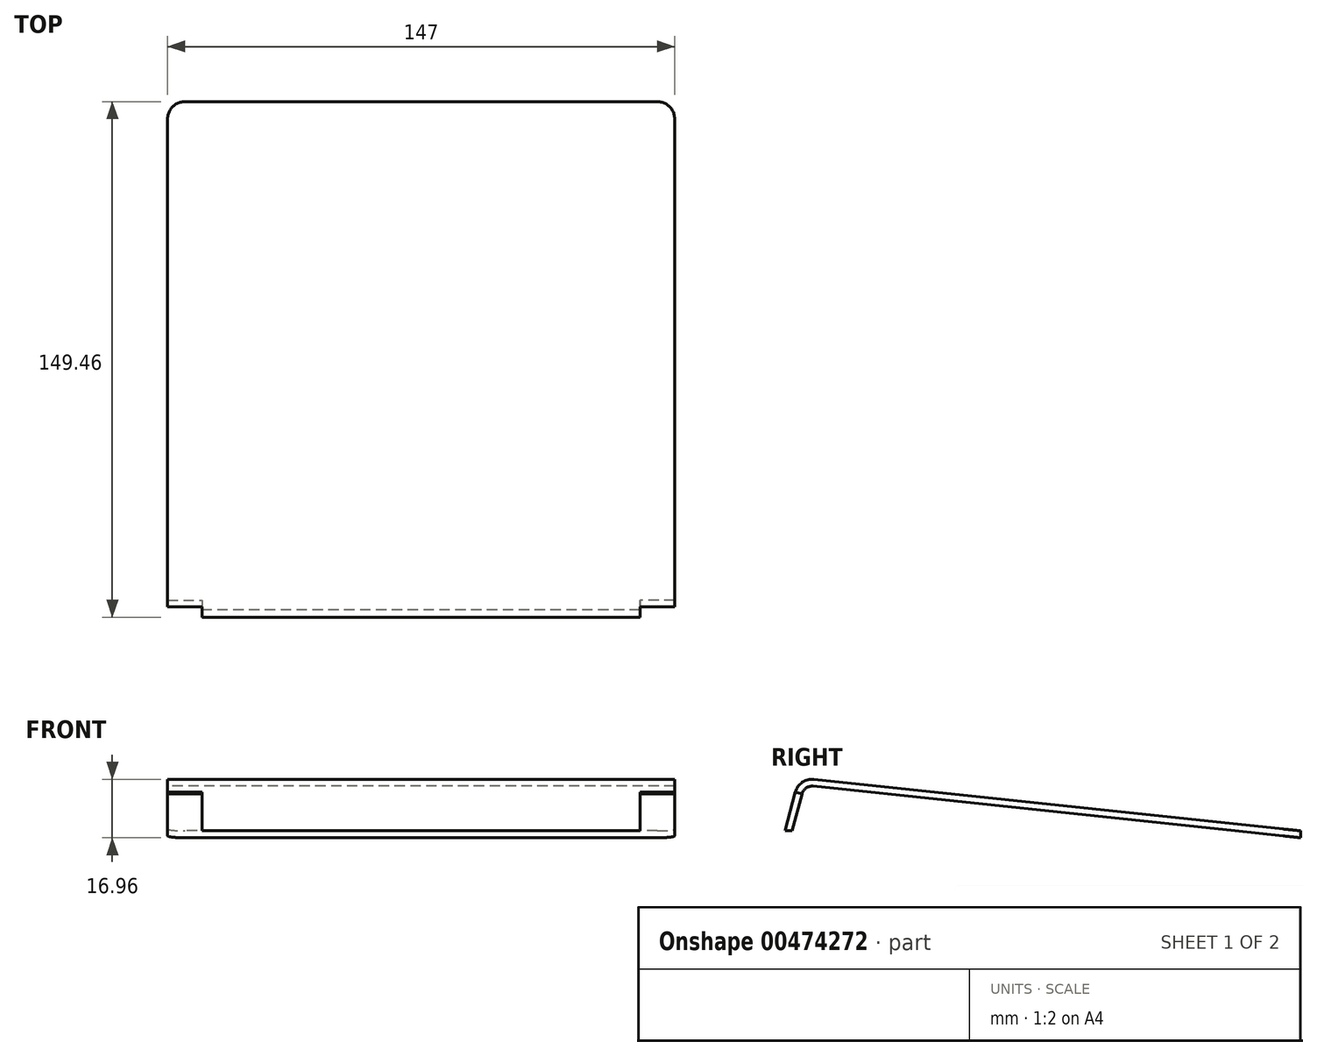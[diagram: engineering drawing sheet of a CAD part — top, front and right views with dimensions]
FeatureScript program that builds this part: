
annotation { "Feature Type Name" : "Feature", "Feature Type Description" : "" }
export const myFeature = defineFeature(function(context is Context, id is Id, definition is map)
    precondition{}
    {
        {
            assignVariable(context, id + "F0", {"name" : "lidWidth", "anyValue" : 129 * mm + 2 * mm});
        }
        {
            assignVariable(context, id + "F1", {"name" : "shellThickness", "anyValue" : 2 * mm});
        }
        {
            var Q0;
            Q0=qCreatedBy(makeId("Right.planeOp"),FACE);
            var sketch = newSketch(context, id + "F2", { "sketchPlane" : qUnion([Q0])});
            skLineSegment(sketch, "E0", {"start": v(-96.45, 13.26) * mm, "end": v(-100, 0) * mm});
            skLineSegment(sketch, "E1", {"start": v(-100, 0) * mm, "end": v(50, 0) * mm});
            skLineSegment(sketch, "E2", {"start": v(50, 0) * mm, "end": v(50, 2) * mm});
            skLineSegment(sketch, "E3", {"start": v(50, 2) * mm, "end": v(-91.1, 16.94) * mm});
            skPoint(sketch, "E4.visualSharp", {"position": v(-95.34, 17.39) * mm});
            skArc(sketch, "E4.filletArc", {"start": v(-91.1, 16.94) * mm, "mid": v(-94.45, 16.09) * mm, "end": v(-96.45, 13.26) * mm});
            skPoint(sketch, "E5", {"position": v(0, 0) * mm});
            skSolve(sketch);
        }
        {
            var Q0;
            Q0 = qSketchRegion(id + "F2", true);
            extrude(context, id + "F3", {"entities" : qUnion([Q0]), "depth" : getVariable(context, 'lidWidth')});
        }
        {
            var Q0;
            Q0=makeQuery(id+"F3.opExtrude","SWEPT_FACE",FACE,{"disambiguationData":[OSD([sQuery(id+"F2.wireOp",EDGE,"E3")])]});
            var Q1;
            Q1=makeQuery(id+"F3.opExtrude","SWEPT_BODY",BODY,{"disambiguationData":[OSD([sQuery(id+"F2.wireOp",EDGE,"E0"),sQuery(id+"F2.wireOp",EDGE,"E2"),sQuery(id+"F2.wireOp",EDGE,"E3"),sQuery(id+"F2.wireOp",EDGE,"E4.filletArc"),sQuery(id+"F2.wireOp",EDGE,"8XllQhxL-LN9K-vVAI-bg7h-7nyJZGlVxFld"),sQuery(id+"F2.wireOp",EDGE,"6OsOoCNm-2A1r-wOlb-xOpm-SVCa7BxokKoD")])]});
            shell(context, id + "F4", {"isHollow" : true, "entities" : qUnion([Q0]), "parts" : qUnion([Q1]), "thickness" : (getVariable(context, 'shellThickness'))});
        }
        {
            var Q0;
            Q0=makeQuery(id+"F3.opExtrude","SWEPT_FACE",FACE,{"disambiguationData":[OSD([sQuery(id+"F2.wireOp",EDGE,"E1")])]});
            extrude(context, id + "F5", {"entities" : qUnion([Q0]), "operationType" : NewBodyOperationType.REMOVE, "oppositeDirection" : true, "depth" : (getVariable(context, 'shellThickness'))});
        }
        {
            var Q0;
            Q0=makeQuery(id+"F3.opExtrude","CAP_FACE",FACE,{"disambiguationData":[OSD([sQuery(id+"F2.wireOp",EDGE,"E0"),sQuery(id+"F2.wireOp",EDGE,"E2"),sQuery(id+"F2.wireOp",EDGE,"E3"),sQuery(id+"F2.wireOp",EDGE,"E4.filletArc"),sQuery(id+"F2.wireOp",EDGE,"8XllQhxL-LN9K-vVAI-bg7h-7nyJZGlVxFld"),sQuery(id+"F2.wireOp",EDGE,"6OsOoCNm-2A1r-wOlb-xOpm-SVCa7BxokKoD")])],"isStart":false});
            extrude(context, id + "F6", {"entities" : qUnion([Q0]), "operationType" : NewBodyOperationType.REMOVE, "oppositeDirection" : true, "depth" : (getVariable(context, 'shellThickness'))});
        }
        {
            var Q0;
            Q0=makeQuery(id+"F3.opExtrude","CAP_FACE",FACE,{"disambiguationData":[OSD([sQuery(id+"F2.wireOp",EDGE,"E0"),sQuery(id+"F2.wireOp",EDGE,"E2"),sQuery(id+"F2.wireOp",EDGE,"E3"),sQuery(id+"F2.wireOp",EDGE,"E4.filletArc"),sQuery(id+"F2.wireOp",EDGE,"8XllQhxL-LN9K-vVAI-bg7h-7nyJZGlVxFld"),sQuery(id+"F2.wireOp",EDGE,"6OsOoCNm-2A1r-wOlb-xOpm-SVCa7BxokKoD")])],"isStart":true});
            extrude(context, id + "F7", {"entities" : qUnion([Q0]), "operationType" : NewBodyOperationType.REMOVE, "oppositeDirection" : true, "depth" : (getVariable(context, 'shellThickness'))});
        }
        {
            var Q0;
            Q0=makeQuery(id+"F6.boolean.opBoolean","COPY",FACE,{"derivedFrom":makeQuery(id+"F6.opExtrude","CAP_FACE",FACE,{"disambiguationData":[OSD([sQuery(id+"F2.wireOp",EDGE,"E0"),sQuery(id+"F2.wireOp",EDGE,"E2"),sQuery(id+"F2.wireOp",EDGE,"E3"),sQuery(id+"F2.wireOp",EDGE,"E4.filletArc"),sQuery(id+"F2.wireOp",EDGE,"8XllQhxL-LN9K-vVAI-bg7h-7nyJZGlVxFld"),sQuery(id+"F2.wireOp",EDGE,"6OsOoCNm-2A1r-wOlb-xOpm-SVCa7BxokKoD")])],"isStart":false})});
            var sketch = newSketch(context, id + "F8", { "sketchPlane" : qUnion([Q0])});
            skLineSegment(sketch, "E6", {"start": v(31, 2) * mm, "end": v(50, 0) * mm});
            skLineSegment(sketch, "E7", {"start": v(50, 0) * mm, "end": v(50, 2) * mm});
            skLineSegment(sketch, "E8", {"start": v(31, 2) * mm, "end": v(50, 2) * mm});
            skSolve(sketch);
        }
        {
            var Q0;
            Q0 = qSketchRegion(id + "F8", true);
            extrude(context, id + "F9", {"entities" : qUnion([Q0]), "oppositeDirection" : true, "depth" : getVariable(context, 'lidWidth') - (getVariable(context, 'shellThickness') * 2)});
        }
        {
            var Q0;
            Q0=makeQuery(id+"F9.opExtrude","SWEPT_BODY",BODY,{"disambiguationData":[OSD([sQuery(id+"F8.wireOp",EDGE,"E6"),sQuery(id+"F8.wireOp",EDGE,"E7"),sQuery(id+"F8.wireOp",EDGE,"E8")])]});
            var Q1;
            Q1=makeQuery(id+"F3.opExtrude","SWEPT_BODY",BODY,{"disambiguationData":[OSD([sQuery(id+"F2.wireOp",EDGE,"E0"),sQuery(id+"F2.wireOp",EDGE,"E2"),sQuery(id+"F2.wireOp",EDGE,"E3"),sQuery(id+"F2.wireOp",EDGE,"E4.filletArc"),sQuery(id+"F2.wireOp",EDGE,"8XllQhxL-LN9K-vVAI-bg7h-7nyJZGlVxFld"),sQuery(id+"F2.wireOp",EDGE,"6OsOoCNm-2A1r-wOlb-xOpm-SVCa7BxokKoD")])]});
            booleanBodies(context, id + "F10", {"operationType" : BooleanOperationType.UNION, "tools" : qUnion([Q0, Q1])});
        }
        {
            var Q0;
            Q0=makeQuery(id+"F13.boolean.opBoolean","MERGE",FACE,{"derivedFrom":[makeQuery(id+"F3.opExtrude","SWEPT_FACE",FACE,{"disambiguationData":[OSD([sQuery(id+"F2.wireOp",EDGE,"E3")])]}),makeQuery(id+"F13.opExtrude","SWEPT_FACE",FACE,{"disambiguationData":[OSD([sQuery(id+"F12.wireOp",EDGE,"E14.0")])]})]});
            var sketch = newSketch(context, id + "F11", { "sketchPlane" : qUnion([Q0])});
            skLineSegment(sketch, "E9", {"start": v(65.5, 49.51) * mm, "end": v(65.5, -92.37) * mm, "construction": true});
            skSolve(sketch);
        }
        {
            var Q0;
            Q0=makeQuery(id+"F10.opBoolean","MERGE",FACE,{"derivedFrom":[makeQuery(id+"F6.boolean.opBoolean","COPY",FACE,{"derivedFrom":makeQuery(id+"F6.opExtrude","CAP_FACE",FACE,{"disambiguationData":[OSD([sQuery(id+"F2.wireOp",EDGE,"E0"),sQuery(id+"F2.wireOp",EDGE,"E1"),sQuery(id+"F2.wireOp",EDGE,"E2"),sQuery(id+"F2.wireOp",EDGE,"E3"),sQuery(id+"F2.wireOp",EDGE,"E4.filletArc")])],"isStart":false})}),makeQuery(id+"F9.opExtrude","CAP_FACE",FACE,{"disambiguationData":[OSD([sQuery(id+"F8.wireOp",EDGE,"E6"),sQuery(id+"F8.wireOp",EDGE,"E7"),sQuery(id+"F8.wireOp",EDGE,"E8")])],"isStart":true})]});
            var sketch = newSketch(context, id + "F12", { "sketchPlane" : qUnion([Q0])});
            skLineSegment(sketch, "E10", {"start": v(-96.45, 13.26) * mm, "end": v(-94.52, 12.74) * mm});
            skLineSegment(sketch, "E11", {"start": v(-91.3, 14.95) * mm, "end": v(-91.1, 16.94) * mm});
            skArc(sketch, "E12.0", {"start": v(-91.1, 16.94) * mm, "mid": v(-94.45, 16.09) * mm, "end": v(-96.45, 13.26) * mm});
            skArc(sketch, "E13.0", {"start": v(-91.3, 14.95) * mm, "mid": v(-93.32, 14.44) * mm, "end": v(-94.52, 12.74) * mm});
            skLineSegment(sketch, "E14.0", {"start": v(50, 2) * mm, "end": v(-91.1, 16.94) * mm});
            skLineSegment(sketch, "E15.0", {"start": v(31, 2) * mm, "end": v(-91.3, 14.95) * mm});
            skSolve(sketch);
        }
        {
            var Q0;
            Q0=makeQuery(id+"F12.imprint","IMPRINT",FACE,{"disambiguationData":[TD([[makeQuery(id+"F12.imprint","IMPRINT",EDGE,{"derivedFrom":sQuery(id+"F12.wireOp",EDGE,"E11")}),-1.0]])]});
            var Q1;
            Q1=makeQuery(id+"F12.imprint","IMPRINT",FACE,{"disambiguationData":[TD([[makeQuery(id+"F12.imprint","IMPRINT",EDGE,{"derivedFrom":sQuery(id+"F12.wireOp",EDGE,"E10")}),1.0]])]});
            extrude(context, id + "F13", {"entities" : qUnion([Q0, Q1]), "operationType" : NewBodyOperationType.ADD, "depth" : 10 * mm});
        }
        {
            var Q0;
            Q0=makeQuery(id+"F10.opBoolean","MERGE",FACE,{"derivedFrom":[makeQuery(id+"F7.boolean.opBoolean","COPY",FACE,{"derivedFrom":makeQuery(id+"F7.opExtrude","CAP_FACE",FACE,{"disambiguationData":[OSD([sQuery(id+"F2.wireOp",EDGE,"E0"),sQuery(id+"F2.wireOp",EDGE,"E1"),sQuery(id+"F2.wireOp",EDGE,"E2"),sQuery(id+"F2.wireOp",EDGE,"E3"),sQuery(id+"F2.wireOp",EDGE,"E4.filletArc")])],"isStart":false})}),makeQuery(id+"F9.opExtrude","CAP_FACE",FACE,{"disambiguationData":[OSD([sQuery(id+"F8.wireOp",EDGE,"E6"),sQuery(id+"F8.wireOp",EDGE,"E7"),sQuery(id+"F8.wireOp",EDGE,"E8")])],"isStart":false})]});
            var sketch = newSketch(context, id + "F14", { "sketchPlane" : qUnion([Q0])});
            skLineSegment(sketch, "E16", {"start": v(94.52, 12.74) * mm, "end": v(96.45, 13.26) * mm});
            skArc(sketch, "E17.0", {"start": v(91.1, 16.94) * mm, "mid": v(94.45, 16.09) * mm, "end": v(96.45, 13.26) * mm});
            skArc(sketch, "E18.0", {"start": v(91.3, 14.95) * mm, "mid": v(93.32, 14.44) * mm, "end": v(94.52, 12.74) * mm});
            skLineSegment(sketch, "E19.0", {"start": v(-50, 2) * mm, "end": v(91.1, 16.94) * mm});
            skLineSegment(sketch, "E20.0", {"start": v(-31, 2) * mm, "end": v(91.3, 14.95) * mm});
            skSolve(sketch);
        }
        {
            var Q0;
            Q0=makeQuery(id+"F14.imprint","IMPRINT",FACE,{"disambiguationData":[TD([[makeQuery(id+"F14.imprint","IMPRINT",EDGE,{"derivedFrom":sQuery(id+"F14.wireOp",EDGE,"E16")}),1.0]])]});
            extrude(context, id + "F15", {"entities" : qUnion([Q0]), "operationType" : NewBodyOperationType.ADD, "depth" : 10 * mm});
        }
        {
            var Q0;
            Q0=makeQuery(id+"F13.opExtrude","CAP_EDGE",EDGE,{"disambiguationData":[OSD([sQuery(id+"F8.wireOp",EDGE,"E7")])],"isStart":false});
            var Q1;
            Q1=makeQuery(id+"F15.opExtrude","CAP_EDGE",EDGE,{"disambiguationData":[OSD([sQuery(id+"F8.wireOp",EDGE,"E7")])],"isStart":false});
            fillet(context, id + "F16", {"entities" : qUnion([Q0, Q1]), "radius" : 5 * mm, "tangentPropagation" : true, "allowEdgeOverflow" : false});
        }
    });
